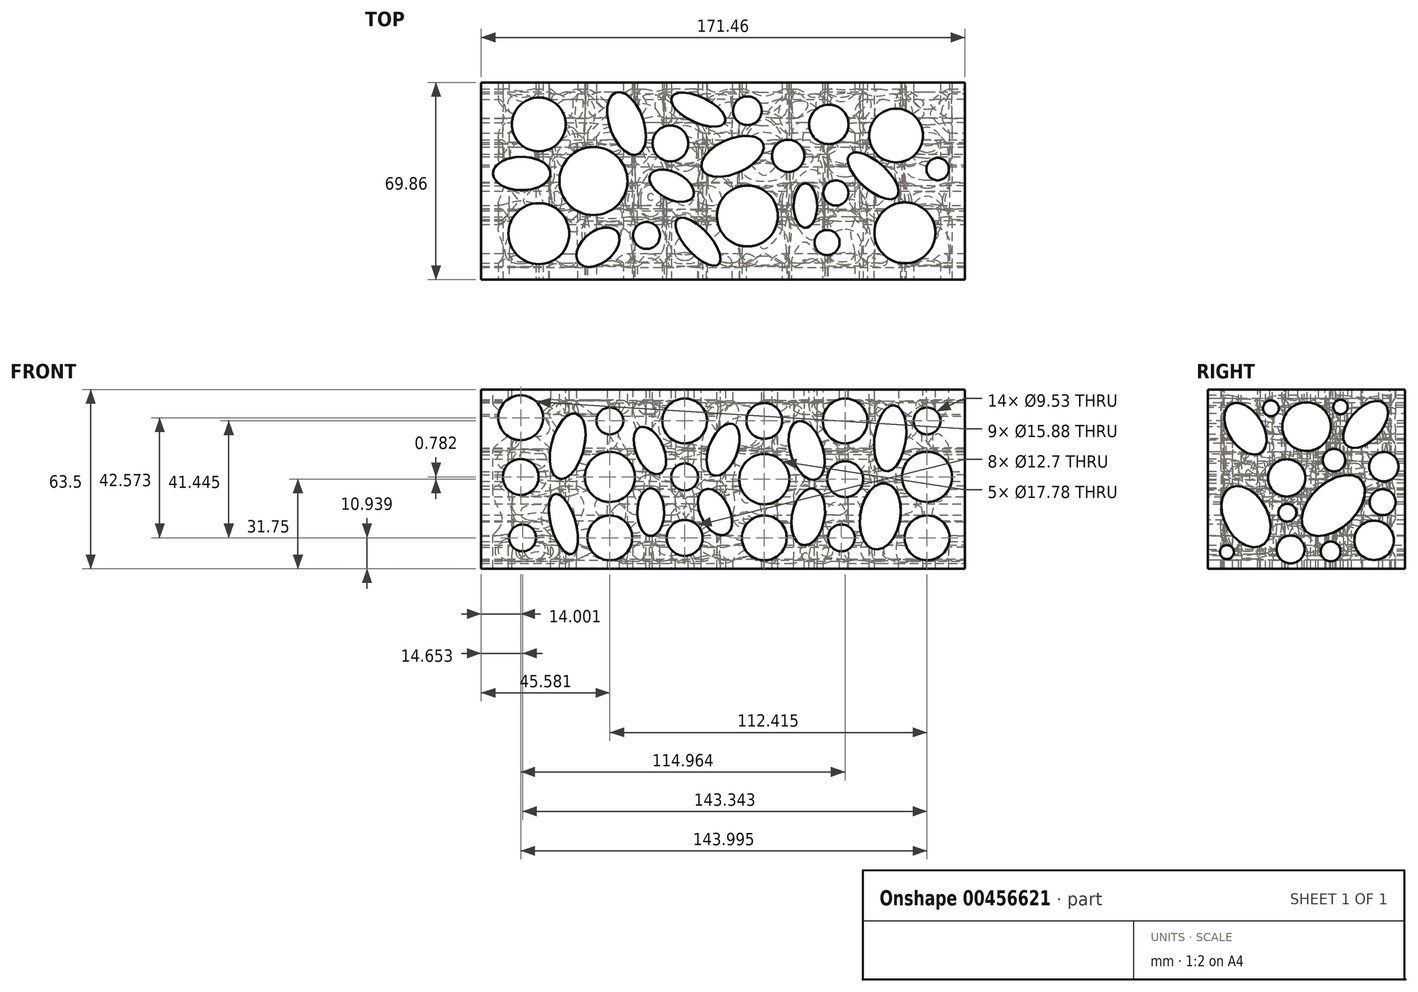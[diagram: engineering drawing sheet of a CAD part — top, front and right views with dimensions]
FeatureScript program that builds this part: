
annotation { "Feature Type Name" : "Feature", "Feature Type Description" : "" }
export const myFeature = defineFeature(function(context is Context, id is Id, definition is map)
    precondition{}
    {
        {
            var Q0;
            Q0=qCreatedBy(makeId("Top.planeOp"),FACE);
            var sketch = newSketch(context, id + "F0", { "sketchPlane" : qUnion([Q0])});
            skLineSegment(sketch, "E0.bottom", {"start": v(-85.73, -34.93) * mm, "end": v(85.73, -34.93) * mm});
            skLineSegment(sketch, "E0.top", {"start": v(-85.73, 34.93) * mm, "end": v(85.73, 34.93) * mm});
            skLineSegment(sketch, "E0.left", {"start": v(-85.73, -34.93) * mm, "end": v(-85.73, 34.93) * mm});
            skLineSegment(sketch, "E0.right", {"start": v(85.73, -34.93) * mm, "end": v(85.73, 34.93) * mm});
            skPoint(sketch, "E0.middle", {"position": v(0, 0) * mm});
            skSolve(sketch);
        }
        {
            var Q0;
            Q0=makeQuery(id+"F0.imprint","IMPRINT",FACE,{"disambiguationData":[TD([[makeQuery(id+"F0.imprint","IMPRINT",EDGE,{"derivedFrom":sQuery(id+"F0.wireOp",EDGE,"E0.bottom")}),1.0]])]});
            extrude(context, id + "F1", {"entities" : qUnion([Q0]), "depth" : 63.5 * mm});
        }
        {
            var Q0;
            Q0=makeQuery(id+"F1.opExtrude","CAP_FACE",FACE,{"disambiguationData":[OSD([sQuery(id+"F0.wireOp",EDGE,"E0.bottom"),sQuery(id+"F0.wireOp",EDGE,"E0.top"),sQuery(id+"F0.wireOp",EDGE,"E0.left"),sQuery(id+"F0.wireOp",EDGE,"E0.right")])],"isStart":false});
            var sketch = newSketch(context, id + "F2", { "sketchPlane" : qUnion([Q0])});
            skCircle(sketch, "E1", {"center": v(-65.32, 20.08) * mm, "radius": 9.53 * mm});
            skCircle(sketch, "E2", {"center": v(-45.96, 0) * mm, "radius": 12.07 * mm});
            skCircle(sketch, "E3", {"center": v(-65.32, -18.64) * mm, "radius": 10.8 * mm});
            skCircle(sketch, "E4", {"center": v(-18.68, 13.32) * mm, "radius": 6.35 * mm});
            skCircle(sketch, "E5", {"center": v(-27.14, -19.3) * mm, "radius": 4.76 * mm});
            skCircle(sketch, "E6", {"center": v(8.6, -12.4) * mm, "radius": 10.8 * mm});
            skCircle(sketch, "E7", {"center": v(23.03, 8.93) * mm, "radius": 5.72 * mm});
            skCircle(sketch, "E8", {"center": v(8.6, 24.92) * mm, "radius": 5.08 * mm});
            skCircle(sketch, "E9", {"center": v(64.43, -18.36) * mm, "radius": 10.8 * mm});
            skCircle(sketch, "E10", {"center": v(76.03, 4.22) * mm, "radius": 3.97 * mm});
            skCircle(sketch, "E11", {"center": v(61.3, 16.14) * mm, "radius": 9.53 * mm});
            skCircle(sketch, "E12", {"center": v(37.46, 20.08) * mm, "radius": 6.99 * mm});
            skCircle(sketch, "E13", {"center": v(39.97, -4.24) * mm, "radius": 4.45 * mm});
            skCircle(sketch, "E14", {"center": v(36.83, -21.8) * mm, "radius": 4.45 * mm});
            skEllipse(sketch, "E15", {"center": v(-18.21, -1.66) * mm, "majorRadius": 8.53 * mm, "minorRadius": 4.78 * mm, "majorAxis": v(0.9, -0.46)});
            skEllipse(sketch, "E16", {"center": v(-8.91, -21.48) * mm, "majorRadius": 10.86 * mm, "minorRadius": 4.4 * mm, "majorAxis": v(-0.67, 0.74)});
            skEllipse(sketch, "E17", {"center": v(3.3, 8.76) * mm, "majorRadius": 11.76 * mm, "minorRadius": 6.1 * mm, "majorAxis": v(0.92, 0.4)});
            skEllipse(sketch, "E18", {"center": v(-34.23, 20.39) * mm, "majorRadius": 11.63 * mm, "minorRadius": 6.05 * mm, "majorAxis": v(-0.33, 0.94)});
            skEllipse(sketch, "E19", {"center": v(-8.8, 25.29) * mm, "majorRadius": 10.4 * mm, "minorRadius": 4.55 * mm, "majorAxis": v(-0.9, 0.43)});
            skEllipse(sketch, "E20", {"center": v(-71.37, 2.66) * mm, "majorRadius": 10.23 * mm, "minorRadius": 5.92 * mm, "majorAxis": v(-1, 0)});
            skEllipse(sketch, "E21", {"center": v(-44.36, -23.45) * mm, "majorRadius": 8.74 * mm, "minorRadius": 5.6 * mm, "majorAxis": v(0.78, 0.63)});
            skEllipse(sketch, "E22", {"center": v(29.16, -8.72) * mm, "majorRadius": 7.88 * mm, "minorRadius": 4.18 * mm, "majorAxis": v(0, 1)});
            skEllipse(sketch, "E23", {"center": v(53.16, 1.84) * mm, "majorRadius": 11.24 * mm, "minorRadius": 4.94 * mm, "majorAxis": v(-0.75, 0.66)});
            skSolve(sketch);
        }
        {
            var Q0;
            Q0=makeQuery(id+"F2.imprint","IMPRINT",FACE,{"disambiguationData":[TD([[makeQuery(id+"F2.imprint","IMPRINT",EDGE,{"derivedFrom":sQuery(id+"F2.wireOp",EDGE,"E1")}),1.0]])]});
            var Q1;
            Q1=makeQuery(id+"F2.imprint","IMPRINT",FACE,{"disambiguationData":[TD([[makeQuery(id+"F2.imprint","IMPRINT",EDGE,{"derivedFrom":sQuery(id+"F2.wireOp",EDGE,"E2")}),1.0]])]});
            var Q2;
            Q2=makeQuery(id+"F2.imprint","IMPRINT",FACE,{"disambiguationData":[TD([[makeQuery(id+"F2.imprint","IMPRINT",EDGE,{"derivedFrom":sQuery(id+"F2.wireOp",EDGE,"E3")}),1.0]])]});
            var Q3;
            Q3=makeQuery(id+"F2.imprint","IMPRINT",FACE,{"disambiguationData":[TD([[makeQuery(id+"F2.imprint","IMPRINT",EDGE,{"derivedFrom":sQuery(id+"F2.wireOp",EDGE,"E11")}),1.0]])]});
            var Q4;
            Q4=makeQuery(id+"F2.imprint","IMPRINT",FACE,{"disambiguationData":[TD([[makeQuery(id+"F2.imprint","IMPRINT",EDGE,{"derivedFrom":sQuery(id+"F2.wireOp",EDGE,"E12")}),1.0]])]});
            var Q5;
            Q5=makeQuery(id+"F2.imprint","IMPRINT",FACE,{"disambiguationData":[TD([[makeQuery(id+"F2.imprint","IMPRINT",EDGE,{"derivedFrom":sQuery(id+"F2.wireOp",EDGE,"E7")}),1.0]])]});
            var Q6;
            Q6=makeQuery(id+"F2.imprint","IMPRINT",FACE,{"disambiguationData":[TD([[makeQuery(id+"F2.imprint","IMPRINT",EDGE,{"derivedFrom":sQuery(id+"F2.wireOp",EDGE,"E8")}),1.0]])]});
            var Q7;
            Q7=makeQuery(id+"F2.imprint","IMPRINT",FACE,{"disambiguationData":[TD([[makeQuery(id+"F2.imprint","IMPRINT",EDGE,{"derivedFrom":sQuery(id+"F2.wireOp",EDGE,"E4")}),1.0]])]});
            var Q8;
            Q8=makeQuery(id+"F2.imprint","IMPRINT",FACE,{"disambiguationData":[TD([[makeQuery(id+"F2.imprint","IMPRINT",EDGE,{"derivedFrom":sQuery(id+"F2.wireOp",EDGE,"E5")}),1.0]])]});
            var Q9;
            Q9=makeQuery(id+"F2.imprint","IMPRINT",FACE,{"disambiguationData":[TD([[makeQuery(id+"F2.imprint","IMPRINT",EDGE,{"derivedFrom":sQuery(id+"F2.wireOp",EDGE,"E6")}),1.0]])]});
            var Q10;
            Q10=makeQuery(id+"F2.imprint","IMPRINT",FACE,{"disambiguationData":[TD([[makeQuery(id+"F2.imprint","IMPRINT",EDGE,{"derivedFrom":sQuery(id+"F2.wireOp",EDGE,"E13")}),1.0]])]});
            var Q11;
            Q11=makeQuery(id+"F2.imprint","IMPRINT",FACE,{"disambiguationData":[TD([[makeQuery(id+"F2.imprint","IMPRINT",EDGE,{"derivedFrom":sQuery(id+"F2.wireOp",EDGE,"E10")}),1.0]])]});
            var Q12;
            Q12=makeQuery(id+"F2.imprint","IMPRINT",FACE,{"disambiguationData":[TD([[makeQuery(id+"F2.imprint","IMPRINT",EDGE,{"derivedFrom":sQuery(id+"F2.wireOp",EDGE,"E9")}),1.0]])]});
            var Q13;
            Q13=makeQuery(id+"F2.imprint","IMPRINT",FACE,{"disambiguationData":[TD([[makeQuery(id+"F2.imprint","IMPRINT",EDGE,{"derivedFrom":sQuery(id+"F2.wireOp",EDGE,"E14")}),1.0]])]});
            var Q14;
            Q14=makeQuery(id+"F2.imprint","IMPRINT",FACE,{"disambiguationData":[TD([[makeQuery(id+"F2.imprint","IMPRINT",EDGE,{"derivedFrom":sQuery(id+"F2.wireOp",EDGE,"E20")}),1.0]])]});
            var Q15;
            Q15=makeQuery(id+"F2.imprint","IMPRINT",FACE,{"disambiguationData":[TD([[makeQuery(id+"F2.imprint","IMPRINT",EDGE,{"derivedFrom":sQuery(id+"F2.wireOp",EDGE,"E21")}),1.0]])]});
            var Q16;
            Q16=makeQuery(id+"F2.imprint","IMPRINT",FACE,{"disambiguationData":[TD([[makeQuery(id+"F2.imprint","IMPRINT",EDGE,{"derivedFrom":sQuery(id+"F2.wireOp",EDGE,"E18")}),1.0]])]});
            var Q17;
            Q17=makeQuery(id+"F2.imprint","IMPRINT",FACE,{"disambiguationData":[TD([[makeQuery(id+"F2.imprint","IMPRINT",EDGE,{"derivedFrom":sQuery(id+"F2.wireOp",EDGE,"E15")}),1.0]])]});
            var Q18;
            Q18=makeQuery(id+"F2.imprint","IMPRINT",FACE,{"disambiguationData":[TD([[makeQuery(id+"F2.imprint","IMPRINT",EDGE,{"derivedFrom":sQuery(id+"F2.wireOp",EDGE,"E16")}),1.0]])]});
            var Q19;
            Q19=makeQuery(id+"F2.imprint","IMPRINT",FACE,{"disambiguationData":[TD([[makeQuery(id+"F2.imprint","IMPRINT",EDGE,{"derivedFrom":sQuery(id+"F2.wireOp",EDGE,"E19")}),1.0]])]});
            var Q20;
            Q20=makeQuery(id+"F2.imprint","IMPRINT",FACE,{"disambiguationData":[TD([[makeQuery(id+"F2.imprint","IMPRINT",EDGE,{"derivedFrom":sQuery(id+"F2.wireOp",EDGE,"E17")}),1.0]])]});
            var Q21;
            Q21=makeQuery(id+"F2.imprint","IMPRINT",FACE,{"disambiguationData":[TD([[makeQuery(id+"F2.imprint","IMPRINT",EDGE,{"derivedFrom":sQuery(id+"F2.wireOp",EDGE,"E22")}),1.0]])]});
            var Q22;
            Q22=makeQuery(id+"F2.imprint","IMPRINT",FACE,{"disambiguationData":[TD([[makeQuery(id+"F2.imprint","IMPRINT",EDGE,{"derivedFrom":sQuery(id+"F2.wireOp",EDGE,"E23")}),1.0]])]});
            var Q23;
            Q23=sQuery(id+"F2.wireOp",EDGE,"E2");
            var Q24;
            Q24=sQuery(id+"F2.wireOp",EDGE,"E1");
            var Q25;
            Q25=sQuery(id+"F2.wireOp",EDGE,"E4");
            var Q26;
            Q26=sQuery(id+"F2.wireOp",EDGE,"E3");
            var Q27;
            Q27=sQuery(id+"F2.wireOp",EDGE,"E5");
            var Q28;
            Q28=sQuery(id+"F2.wireOp",EDGE,"E6");
            var Q29;
            Q29=sQuery(id+"F2.wireOp",EDGE,"E14");
            var Q30;
            Q30=sQuery(id+"F2.wireOp",EDGE,"E9");
            var Q31;
            Q31=sQuery(id+"F2.wireOp",EDGE,"E10");
            var Q32;
            Q32=sQuery(id+"F2.wireOp",EDGE,"E13");
            var Q33;
            Q33=sQuery(id+"F2.wireOp",EDGE,"E11");
            var Q34;
            Q34=sQuery(id+"F2.wireOp",EDGE,"E12");
            var Q35;
            Q35=sQuery(id+"F2.wireOp",EDGE,"E7");
            var Q36;
            Q36=sQuery(id+"F2.wireOp",EDGE,"E8");
            extrude(context, id + "F3", {"entities" : qUnion([Q0, Q1, Q2, Q3, Q4, Q5, Q6, Q7, Q8, Q9, Q10, Q11, Q12, Q13, Q14, Q15, Q16, Q17, Q18, Q19, Q20, Q21, Q22]), "operationType" : NewBodyOperationType.REMOVE, "surfaceEntities" : qUnion([Q23, Q24, Q25, Q26, Q27, Q28, Q29, Q30, Q31, Q32, Q33, Q34, Q35, Q36]), "endBound" : BoundingType.THROUGH_ALL, "oppositeDirection" : true, "depth" : 25.4 * mm});
        }
        {
            var Q0;
            Q0=makeQuery(id+"F1.opExtrude","SWEPT_FACE",FACE,{"disambiguationData":[OSD([sQuery(id+"F0.wireOp",EDGE,"E0.bottom")])]});
            var sketch = newSketch(context, id + "F4", { "sketchPlane" : qUnion([Q0])});
            skCircle(sketch, "E24", {"center": v(-71.73, 53.51) * mm, "radius": 7.94 * mm});
            skCircle(sketch, "E25", {"center": v(-40.15, 10.94) * mm, "radius": 7.94 * mm});
            skCircle(sketch, "E26", {"center": v(-13.62, 52.38) * mm, "radius": 7.94 * mm});
            skCircle(sketch, "E27", {"center": v(14.59, 10.94) * mm, "radius": 7.94 * mm});
            skCircle(sketch, "E28", {"center": v(43.24, 52.38) * mm, "radius": 7.94 * mm});
            skCircle(sketch, "E29", {"center": v(72.27, 10.94) * mm, "radius": 7.94 * mm});
            skCircle(sketch, "E30", {"center": v(-71.08, 10.94) * mm, "radius": 4.76 * mm});
            skCircle(sketch, "E31", {"center": v(-40.15, 52.38) * mm, "radius": 4.76 * mm});
            skCircle(sketch, "E32", {"center": v(-13.62, 32.53) * mm, "radius": 4.76 * mm});
            skCircle(sketch, "E33", {"center": v(41.9, 10.94) * mm, "radius": 4.76 * mm});
            skCircle(sketch, "E34", {"center": v(72.27, 52.38) * mm, "radius": 4.76 * mm});
            skCircle(sketch, "E35", {"center": v(43.24, 31.75) * mm, "radius": 6.35 * mm});
            skCircle(sketch, "E36", {"center": v(14.59, 52.38) * mm, "radius": 6.35 * mm});
            skCircle(sketch, "E37", {"center": v(-13.62, 10.94) * mm, "radius": 6.35 * mm});
            skCircle(sketch, "E38", {"center": v(-71.73, 32.53) * mm, "radius": 6.35 * mm});
            skCircle(sketch, "E39", {"center": v(72.27, 32.53) * mm, "radius": 8.9 * mm});
            skCircle(sketch, "E40", {"center": v(-40.15, 32.53) * mm, "radius": 8.9 * mm});
            skCircle(sketch, "E41", {"center": v(14.59, 31.75) * mm, "radius": 8.9 * mm});
            skEllipse(sketch, "E42", {"center": v(-55.1, 43.44) * mm, "majorRadius": 11.93 * mm, "minorRadius": 5.78 * mm, "majorAxis": v(0.25, 0.97)});
            skEllipse(sketch, "E43", {"center": v(-56.62, 15.81) * mm, "majorRadius": 11.05 * mm, "minorRadius": 4.34 * mm, "majorAxis": v(0.27, -0.96)});
            skEllipse(sketch, "E44", {"center": v(-25.65, 20.06) * mm, "majorRadius": 8.5 * mm, "minorRadius": 4.77 * mm, "majorAxis": v(0, 1)});
            skEllipse(sketch, "E45", {"center": v(-25.96, 41.92) * mm, "majorRadius": 8.97 * mm, "minorRadius": 4.9 * mm, "majorAxis": v(-0.4, 0.91)});
            skEllipse(sketch, "E46", {"center": v(0, 42.22) * mm, "majorRadius": 9.75 * mm, "minorRadius": 5.05 * mm, "majorAxis": v(0.36, 0.93)});
            skEllipse(sketch, "E47", {"center": v(-2.88, 20.06) * mm, "majorRadius": 8.82 * mm, "minorRadius": 5.17 * mm, "majorAxis": v(-0.45, 0.9)});
            skEllipse(sketch, "E48", {"center": v(29.6, 41.92) * mm, "majorRadius": 10.85 * mm, "minorRadius": 5.73 * mm, "majorAxis": v(-0.3, 0.95)});
            skEllipse(sketch, "E49", {"center": v(30.15, 18.39) * mm, "majorRadius": 10.18 * mm, "minorRadius": 5.78 * mm, "majorAxis": v(0.19, 0.98)});
            skEllipse(sketch, "E50", {"center": v(55.7, 18.57) * mm, "majorRadius": 11.84 * mm, "minorRadius": 7.15 * mm, "majorAxis": v(0.16, 0.99)});
            skEllipse(sketch, "E51", {"center": v(59.2, 46.24) * mm, "majorRadius": 11.79 * mm, "minorRadius": 5.56 * mm, "majorAxis": v(0.13, 1)});
            skSolve(sketch);
        }
        {
            var Q0;
            Q0=makeQuery(id+"F4.imprint","IMPRINT",FACE,{"disambiguationData":[TD([[makeQuery(id+"F4.imprint","IMPRINT",EDGE,{"derivedFrom":sQuery(id+"F4.wireOp",EDGE,"E24")}),1.0]])]});
            var Q1;
            Q1=makeQuery(id+"F4.imprint","IMPRINT",FACE,{"disambiguationData":[TD([[makeQuery(id+"F4.imprint","IMPRINT",EDGE,{"derivedFrom":sQuery(id+"F4.wireOp",EDGE,"E31")}),1.0]])]});
            var Q2;
            Q2=makeQuery(id+"F4.imprint","IMPRINT",FACE,{"disambiguationData":[TD([[makeQuery(id+"F4.imprint","IMPRINT",EDGE,{"derivedFrom":sQuery(id+"F4.wireOp",EDGE,"E26")}),1.0]])]});
            var Q3;
            Q3=makeQuery(id+"F4.imprint","IMPRINT",FACE,{"disambiguationData":[TD([[makeQuery(id+"F4.imprint","IMPRINT",EDGE,{"derivedFrom":sQuery(id+"F4.wireOp",EDGE,"E36")}),1.0]])]});
            var Q4;
            Q4=makeQuery(id+"F4.imprint","IMPRINT",FACE,{"disambiguationData":[TD([[makeQuery(id+"F4.imprint","IMPRINT",EDGE,{"derivedFrom":sQuery(id+"F4.wireOp",EDGE,"E28")}),1.0]])]});
            var Q5;
            Q5=makeQuery(id+"F4.imprint","IMPRINT",FACE,{"disambiguationData":[TD([[makeQuery(id+"F4.imprint","IMPRINT",EDGE,{"derivedFrom":sQuery(id+"F4.wireOp",EDGE,"E34")}),1.0]])]});
            var Q6;
            Q6=makeQuery(id+"F4.imprint","IMPRINT",FACE,{"disambiguationData":[TD([[makeQuery(id+"F4.imprint","IMPRINT",EDGE,{"derivedFrom":sQuery(id+"F4.wireOp",EDGE,"E39")}),1.0]])]});
            var Q7;
            Q7=makeQuery(id+"F4.imprint","IMPRINT",FACE,{"disambiguationData":[TD([[makeQuery(id+"F4.imprint","IMPRINT",EDGE,{"derivedFrom":sQuery(id+"F4.wireOp",EDGE,"E29")}),1.0]])]});
            var Q8;
            Q8=makeQuery(id+"F4.imprint","IMPRINT",FACE,{"disambiguationData":[TD([[makeQuery(id+"F4.imprint","IMPRINT",EDGE,{"derivedFrom":sQuery(id+"F4.wireOp",EDGE,"E33")}),1.0]])]});
            var Q9;
            Q9=makeQuery(id+"F4.imprint","IMPRINT",FACE,{"disambiguationData":[TD([[makeQuery(id+"F4.imprint","IMPRINT",EDGE,{"derivedFrom":sQuery(id+"F4.wireOp",EDGE,"E35")}),1.0]])]});
            var Q10;
            Q10=makeQuery(id+"F4.imprint","IMPRINT",FACE,{"disambiguationData":[TD([[makeQuery(id+"F4.imprint","IMPRINT",EDGE,{"derivedFrom":sQuery(id+"F4.wireOp",EDGE,"E41")}),1.0]])]});
            var Q11;
            Q11=makeQuery(id+"F4.imprint","IMPRINT",FACE,{"disambiguationData":[TD([[makeQuery(id+"F4.imprint","IMPRINT",EDGE,{"derivedFrom":sQuery(id+"F4.wireOp",EDGE,"E27")}),1.0]])]});
            var Q12;
            Q12=makeQuery(id+"F4.imprint","IMPRINT",FACE,{"disambiguationData":[TD([[makeQuery(id+"F4.imprint","IMPRINT",EDGE,{"derivedFrom":sQuery(id+"F4.wireOp",EDGE,"E37")}),1.0]])]});
            var Q13;
            Q13=makeQuery(id+"F4.imprint","IMPRINT",FACE,{"disambiguationData":[TD([[makeQuery(id+"F4.imprint","IMPRINT",EDGE,{"derivedFrom":sQuery(id+"F4.wireOp",EDGE,"E32")}),1.0]])]});
            var Q14;
            Q14=makeQuery(id+"F4.imprint","IMPRINT",FACE,{"disambiguationData":[TD([[makeQuery(id+"F4.imprint","IMPRINT",EDGE,{"derivedFrom":sQuery(id+"F4.wireOp",EDGE,"E25")}),1.0]])]});
            var Q15;
            Q15=makeQuery(id+"F4.imprint","IMPRINT",FACE,{"disambiguationData":[TD([[makeQuery(id+"F4.imprint","IMPRINT",EDGE,{"derivedFrom":sQuery(id+"F4.wireOp",EDGE,"E30")}),1.0]])]});
            var Q16;
            Q16=makeQuery(id+"F4.imprint","IMPRINT",FACE,{"disambiguationData":[TD([[makeQuery(id+"F4.imprint","IMPRINT",EDGE,{"derivedFrom":sQuery(id+"F4.wireOp",EDGE,"E38")}),1.0]])]});
            var Q17;
            Q17=makeQuery(id+"F4.imprint","IMPRINT",FACE,{"disambiguationData":[TD([[makeQuery(id+"F4.imprint","IMPRINT",EDGE,{"derivedFrom":sQuery(id+"F4.wireOp",EDGE,"E40")}),1.0]])]});
            var Q18;
            Q18=makeQuery(id+"F4.imprint","IMPRINT",FACE,{"disambiguationData":[TD([[makeQuery(id+"F4.imprint","IMPRINT",EDGE,{"derivedFrom":sQuery(id+"F4.wireOp",EDGE,"E51")}),1.0]])]});
            var Q19;
            Q19=makeQuery(id+"F4.imprint","IMPRINT",FACE,{"disambiguationData":[TD([[makeQuery(id+"F4.imprint","IMPRINT",EDGE,{"derivedFrom":sQuery(id+"F4.wireOp",EDGE,"E50")}),1.0]])]});
            var Q20;
            Q20=makeQuery(id+"F4.imprint","IMPRINT",FACE,{"disambiguationData":[TD([[makeQuery(id+"F4.imprint","IMPRINT",EDGE,{"derivedFrom":sQuery(id+"F4.wireOp",EDGE,"E49")}),1.0]])]});
            var Q21;
            Q21=makeQuery(id+"F4.imprint","IMPRINT",FACE,{"disambiguationData":[TD([[makeQuery(id+"F4.imprint","IMPRINT",EDGE,{"derivedFrom":sQuery(id+"F4.wireOp",EDGE,"E48")}),1.0]])]});
            var Q22;
            Q22=makeQuery(id+"F4.imprint","IMPRINT",FACE,{"disambiguationData":[TD([[makeQuery(id+"F4.imprint","IMPRINT",EDGE,{"derivedFrom":sQuery(id+"F4.wireOp",EDGE,"E46")}),1.0]])]});
            var Q23;
            Q23=makeQuery(id+"F4.imprint","IMPRINT",FACE,{"disambiguationData":[TD([[makeQuery(id+"F4.imprint","IMPRINT",EDGE,{"derivedFrom":sQuery(id+"F4.wireOp",EDGE,"E47")}),1.0]])]});
            var Q24;
            Q24=makeQuery(id+"F4.imprint","IMPRINT",FACE,{"disambiguationData":[TD([[makeQuery(id+"F4.imprint","IMPRINT",EDGE,{"derivedFrom":sQuery(id+"F4.wireOp",EDGE,"E45")}),1.0]])]});
            var Q25;
            Q25=makeQuery(id+"F4.imprint","IMPRINT",FACE,{"disambiguationData":[TD([[makeQuery(id+"F4.imprint","IMPRINT",EDGE,{"derivedFrom":sQuery(id+"F4.wireOp",EDGE,"E44")}),1.0]])]});
            var Q26;
            Q26=makeQuery(id+"F4.imprint","IMPRINT",FACE,{"disambiguationData":[TD([[makeQuery(id+"F4.imprint","IMPRINT",EDGE,{"derivedFrom":sQuery(id+"F4.wireOp",EDGE,"E43")}),1.0]])]});
            var Q27;
            Q27=makeQuery(id+"F4.imprint","IMPRINT",FACE,{"disambiguationData":[TD([[makeQuery(id+"F4.imprint","IMPRINT",EDGE,{"derivedFrom":sQuery(id+"F4.wireOp",EDGE,"E42")}),1.0]])]});
            extrude(context, id + "F5", {"entities" : qUnion([Q0, Q1, Q2, Q3, Q4, Q5, Q6, Q7, Q8, Q9, Q10, Q11, Q12, Q13, Q14, Q15, Q16, Q17, Q18, Q19, Q20, Q21, Q22, Q23, Q24, Q25, Q26, Q27]), "operationType" : NewBodyOperationType.REMOVE, "endBound" : BoundingType.THROUGH_ALL, "oppositeDirection" : true, "depth" : 25.4 * mm});
        }
        {
            var Q0;
            Q0=makeQuery(id+"F1.opExtrude","SWEPT_FACE",FACE,{"disambiguationData":[OSD([sQuery(id+"F0.wireOp",EDGE,"E0.right")])]});
            var sketch = newSketch(context, id + "F6", { "sketchPlane" : qUnion([Q0])});
            skEllipse(sketch, "E52", {"center": v(-21.65, 49.61) * mm, "majorRadius": 10.14 * mm, "minorRadius": 6.13 * mm, "majorAxis": v(-0.54, 0.84)});
            skEllipse(sketch, "E53", {"center": v(20.96, 51.14) * mm, "majorRadius": 10.02 * mm, "minorRadius": 5.68 * mm, "majorAxis": v(0.67, 0.74)});
            skEllipse(sketch, "E54", {"center": v(9.5, 22.42) * mm, "majorRadius": 13.34 * mm, "minorRadius": 8.07 * mm, "majorAxis": v(-0.73, -0.68)});
            skEllipse(sketch, "E55", {"center": v(-21.46, 18.46) * mm, "majorRadius": 11.67 * mm, "minorRadius": 7.64 * mm, "majorAxis": v(-0.48, 0.88)});
            skCircle(sketch, "E56", {"center": v(0, 50.35) * mm, "radius": 8.6 * mm});
            skCircle(sketch, "E57", {"center": v(-7.03, 32.2) * mm, "radius": 6.62 * mm});
            skCircle(sketch, "E58", {"center": v(23.94, 10.08) * mm, "radius": 6.99 * mm});
            skCircle(sketch, "E59", {"center": v(27.43, 36.15) * mm, "radius": 5.2 * mm});
            skCircle(sketch, "E60", {"center": v(9.74, 38.48) * mm, "radius": 4 * mm});
            skCircle(sketch, "E61", {"center": v(-25.88, 35.45) * mm, "radius": 4.27 * mm});
            skCircle(sketch, "E62", {"center": v(-5.63, 6.82) * mm, "radius": 4.93 * mm});
            skCircle(sketch, "E63", {"center": v(-6.8, 19.85) * mm, "radius": 3.17 * mm});
            skCircle(sketch, "E64", {"center": v(26.97, 23.58) * mm, "radius": 4.6 * mm});
            skCircle(sketch, "E65", {"center": v(12.07, 57.34) * mm, "radius": 2.56 * mm});
            skCircle(sketch, "E66", {"center": v(8.57, 6.12) * mm, "radius": 3.5 * mm});
            skCircle(sketch, "E67", {"center": v(-28.21, 5.89) * mm, "radius": 2.47 * mm});
            skCircle(sketch, "E68", {"center": v(-12.61, 56.87) * mm, "radius": 2.8 * mm});
            skSolve(sketch);
        }
        {
            var Q0;
            Q0=makeQuery(id+"F6.imprint","IMPRINT",FACE,{"disambiguationData":[TD([[makeQuery(id+"F6.imprint","IMPRINT",EDGE,{"derivedFrom":sQuery(id+"F6.wireOp",EDGE,"E52")}),1.0]])]});
            var Q1;
            Q1=makeQuery(id+"F6.imprint","IMPRINT",FACE,{"disambiguationData":[TD([[makeQuery(id+"F6.imprint","IMPRINT",EDGE,{"derivedFrom":sQuery(id+"F6.wireOp",EDGE,"E56")}),1.0]])]});
            var Q2;
            Q2=makeQuery(id+"F6.imprint","IMPRINT",FACE,{"disambiguationData":[TD([[makeQuery(id+"F6.imprint","IMPRINT",EDGE,{"derivedFrom":sQuery(id+"F6.wireOp",EDGE,"E65")}),1.0]])]});
            var Q3;
            Q3=makeQuery(id+"F6.imprint","IMPRINT",FACE,{"disambiguationData":[TD([[makeQuery(id+"F6.imprint","IMPRINT",EDGE,{"derivedFrom":sQuery(id+"F6.wireOp",EDGE,"E68")}),1.0]])]});
            var Q4;
            Q4=makeQuery(id+"F6.imprint","IMPRINT",FACE,{"disambiguationData":[TD([[makeQuery(id+"F6.imprint","IMPRINT",EDGE,{"derivedFrom":sQuery(id+"F6.wireOp",EDGE,"E53")}),1.0]])]});
            var Q5;
            Q5=makeQuery(id+"F6.imprint","IMPRINT",FACE,{"disambiguationData":[TD([[makeQuery(id+"F6.imprint","IMPRINT",EDGE,{"derivedFrom":sQuery(id+"F6.wireOp",EDGE,"E59")}),1.0]])]});
            var Q6;
            Q6=makeQuery(id+"F6.imprint","IMPRINT",FACE,{"disambiguationData":[TD([[makeQuery(id+"F6.imprint","IMPRINT",EDGE,{"derivedFrom":sQuery(id+"F6.wireOp",EDGE,"E60")}),1.0]])]});
            var Q7;
            Q7=makeQuery(id+"F6.imprint","IMPRINT",FACE,{"disambiguationData":[TD([[makeQuery(id+"F6.imprint","IMPRINT",EDGE,{"derivedFrom":sQuery(id+"F6.wireOp",EDGE,"E57")}),1.0]])]});
            var Q8;
            Q8=makeQuery(id+"F6.imprint","IMPRINT",FACE,{"disambiguationData":[TD([[makeQuery(id+"F6.imprint","IMPRINT",EDGE,{"derivedFrom":sQuery(id+"F6.wireOp",EDGE,"E64")}),1.0]])]});
            var Q9;
            Q9=makeQuery(id+"F6.imprint","IMPRINT",FACE,{"disambiguationData":[TD([[makeQuery(id+"F6.imprint","IMPRINT",EDGE,{"derivedFrom":sQuery(id+"F6.wireOp",EDGE,"E54")}),1.0]])]});
            var Q10;
            Q10=makeQuery(id+"F6.imprint","IMPRINT",FACE,{"disambiguationData":[TD([[makeQuery(id+"F6.imprint","IMPRINT",EDGE,{"derivedFrom":sQuery(id+"F6.wireOp",EDGE,"E63")}),1.0]])]});
            var Q11;
            Q11=makeQuery(id+"F6.imprint","IMPRINT",FACE,{"disambiguationData":[TD([[makeQuery(id+"F6.imprint","IMPRINT",EDGE,{"derivedFrom":sQuery(id+"F6.wireOp",EDGE,"E55")}),1.0]])]});
            var Q12;
            Q12=makeQuery(id+"F6.imprint","IMPRINT",FACE,{"disambiguationData":[TD([[makeQuery(id+"F6.imprint","IMPRINT",EDGE,{"derivedFrom":sQuery(id+"F6.wireOp",EDGE,"E62")}),1.0]])]});
            var Q13;
            Q13=makeQuery(id+"F6.imprint","IMPRINT",FACE,{"disambiguationData":[TD([[makeQuery(id+"F6.imprint","IMPRINT",EDGE,{"derivedFrom":sQuery(id+"F6.wireOp",EDGE,"E67")}),1.0]])]});
            var Q14;
            Q14=makeQuery(id+"F6.imprint","IMPRINT",FACE,{"disambiguationData":[TD([[makeQuery(id+"F6.imprint","IMPRINT",EDGE,{"derivedFrom":sQuery(id+"F6.wireOp",EDGE,"E66")}),1.0]])]});
            var Q15;
            Q15=makeQuery(id+"F6.imprint","IMPRINT",FACE,{"disambiguationData":[TD([[makeQuery(id+"F6.imprint","IMPRINT",EDGE,{"derivedFrom":sQuery(id+"F6.wireOp",EDGE,"E58")}),1.0]])]});
            extrude(context, id + "F7", {"entities" : qUnion([Q0, Q1, Q2, Q3, Q4, Q5, Q6, Q7, Q8, Q9, Q10, Q11, Q12, Q13, Q14, Q15]), "operationType" : NewBodyOperationType.REMOVE, "endBound" : BoundingType.THROUGH_ALL, "oppositeDirection" : true, "depth" : 25.4 * mm});
        }
    });
